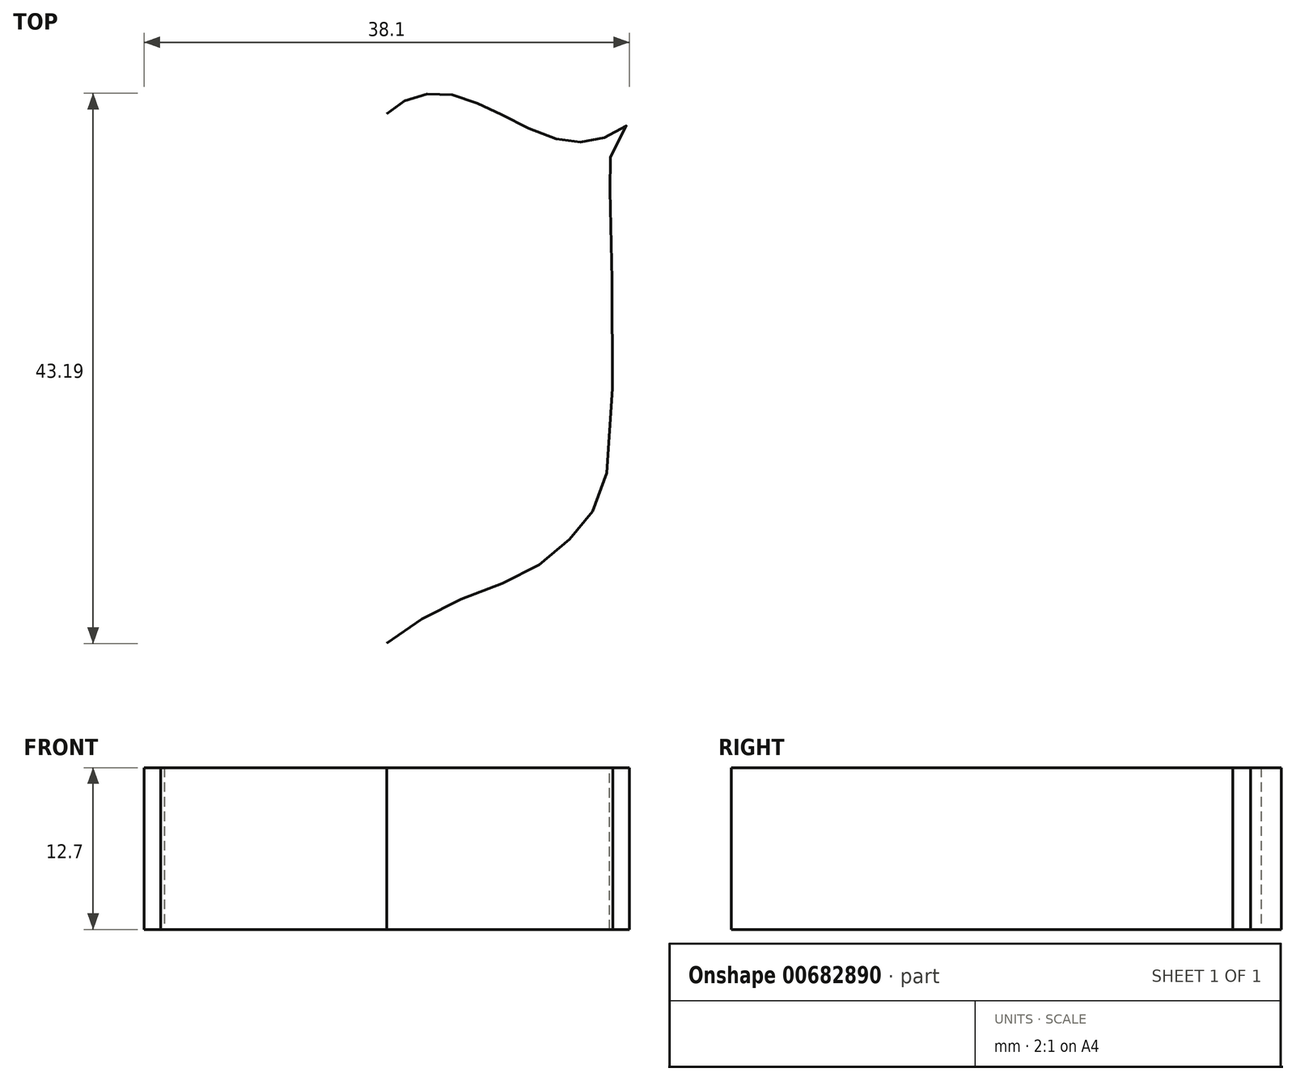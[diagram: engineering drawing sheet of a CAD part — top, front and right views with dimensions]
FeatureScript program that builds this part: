
annotation { "Feature Type Name" : "Feature", "Feature Type Description" : "" }
export const myFeature = defineFeature(function(context is Context, id is Id, definition is map)
    precondition{}
    {
        {
            var Q0;
            Q0=qCreatedBy(makeId("Top.planeOp"),FACE);
            var sketch = newSketch(context, id + "F0", { "sketchPlane" : qUnion([Q0])});
            skLineSegment(sketch, "E0.bottom", {"start": v(-19.05, 25.4) * mm, "end": v(19.05, 25.4) * mm});
            skLineSegment(sketch, "E0.top", {"start": v(-19.05, -25.4) * mm, "end": v(19.05, -25.4) * mm});
            skLineSegment(sketch, "E0.left", {"start": v(-19.05, 25.4) * mm, "end": v(-19.05, -25.4) * mm});
            skLineSegment(sketch, "E0.right", {"start": v(19.05, 25.4) * mm, "end": v(19.05, -25.4) * mm});
            skPoint(sketch, "E0.middle", {"position": v(0, 0) * mm});
            skSolve(sketch);
        }
        {
            var Q0;
            Q0=makeQuery(id+"F0.imprint","IMPRINT",FACE,{"disambiguationData":[TD([[makeQuery(id+"F0.imprint","IMPRINT",EDGE,{"derivedFrom":sQuery(id+"F0.wireOp",EDGE,"E0.bottom")}),-1.0]])]});
            var sketch = newSketch(context, id + "F1", { "sketchPlane" : qUnion([Q0])});
            skFitSpline(sketch, "E1", {"points": [v(0, 20.09) * mm, v(-1, 20.84) * mm, v(-2.24, 21.45) * mm, v(-4.01, 21.7) * mm, v(-5.6, 21.47) * mm, v(-7.47, 20.74) * mm, v(-9.25, 19.91) * mm, v(-11.53, 18.76) * mm, v(-13.6, 18.03) * mm, v(-15.15, 17.86) * mm, v(-16.78, 18.1) * mm, v(-18.28, 18.8) * mm, v(-19.04, 19.26) * mm, v(-18.3, 18.25) * mm, v(-17.59, 16.81) * mm, v(-17.48, 15.3) * mm, v(-17.37, -7.44) * mm, v(-15.72, -11.73) * mm, v(-13.02, -14.56) * mm, v(-9.08, -16.77) * mm, v(-4.18, -18.77) * mm, v(0, -21.5) * mm], "startDerivative": vector(-23.91, 21.84) * mm, "endDerivative": vector(61.86, -45.52) * mm});
            skFitSpline(sketch, "E2.MirrorCS", {"points": [v(0, 20.09) * mm, v(1, 20.84) * mm, v(2.24, 21.45) * mm, v(4.01, 21.7) * mm, v(5.6, 21.47) * mm, v(7.47, 20.74) * mm, v(9.25, 19.91) * mm, v(11.53, 18.76) * mm, v(13.6, 18.03) * mm, v(15.15, 17.86) * mm, v(16.78, 18.1) * mm, v(18.28, 18.8) * mm, v(19.04, 19.26) * mm, v(18.3, 18.25) * mm, v(17.59, 16.81) * mm, v(17.48, 15.3) * mm, v(17.37, -7.44) * mm, v(15.72, -11.73) * mm, v(13.02, -14.56) * mm, v(9.08, -16.77) * mm, v(4.18, -18.77) * mm, v(0, -21.5) * mm], "startDerivative": vector(23.91, 21.84) * mm, "endDerivative": vector(-61.86, -45.52) * mm});
            skSolve(sketch);
        }
        {
            var Q0;
            Q0 = qSketchRegion(id + "F1", true);
            extrude(context, id + "F2", {"entities" : qUnion([Q0]), "depth" : 12.7 * mm, "offsetDistance" : 25.4 * mm});
        }
    });
